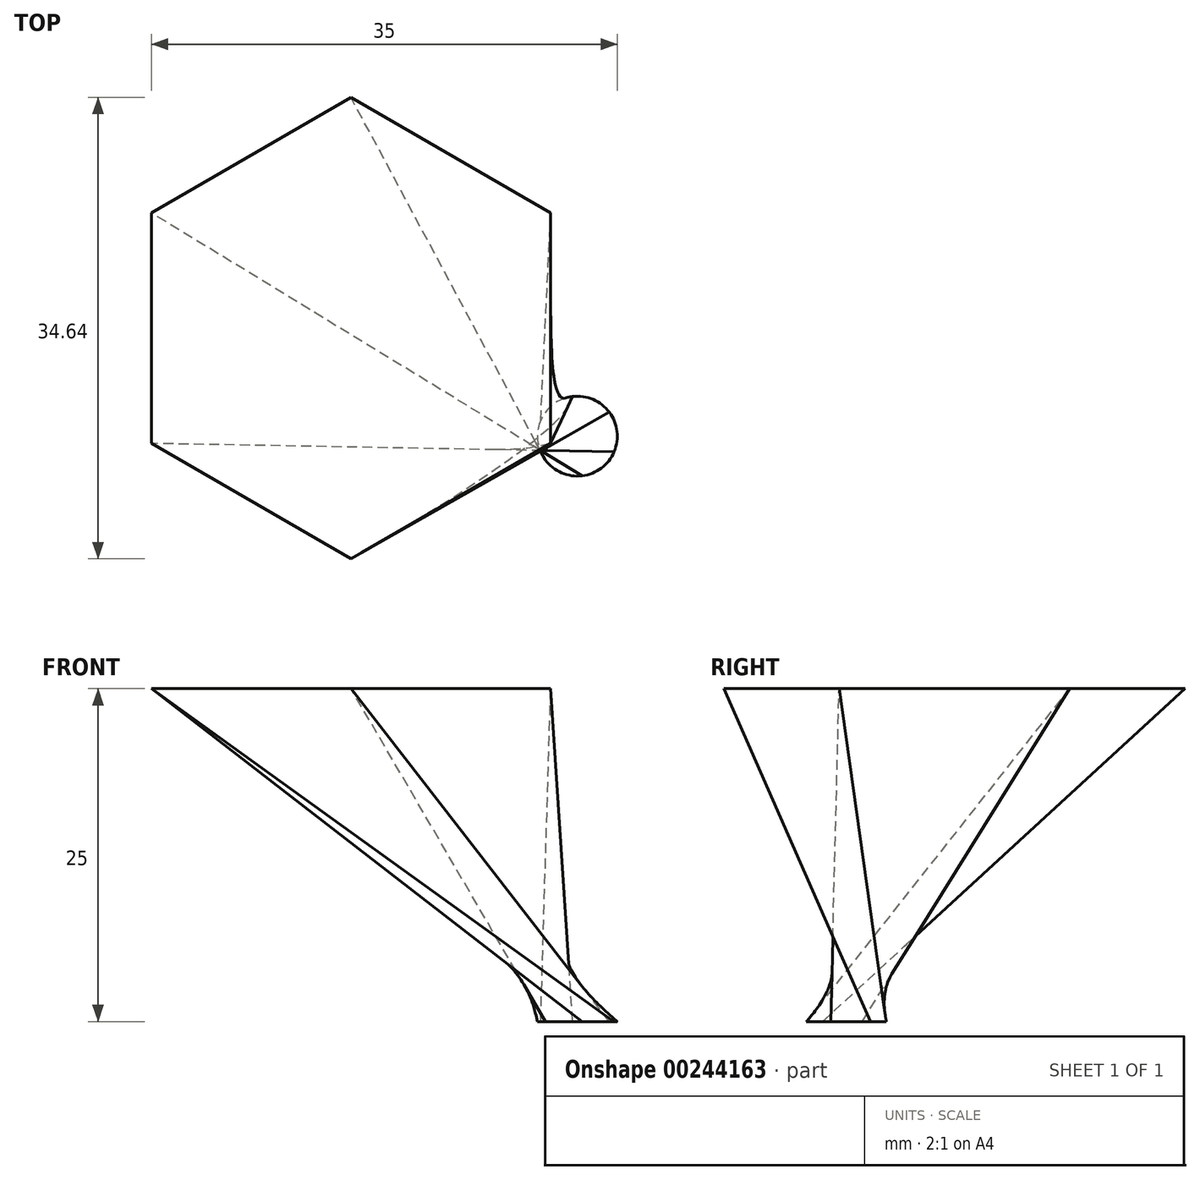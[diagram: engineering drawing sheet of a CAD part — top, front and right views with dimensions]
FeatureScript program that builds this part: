
annotation { "Feature Type Name" : "Feature", "Feature Type Description" : "" }
export const myFeature = defineFeature(function(context is Context, id is Id, definition is map)
    precondition{}
    {
        {
            var Q0;
            Q0=qCreatedBy(makeId("Top.planeOp"),FACE);
            var sketch = newSketch(context, id + "F0", { "sketchPlane" : qUnion([Q0])});
            skCircle(sketch, "E0", {"center": v(17, -8.11) * mm, "radius": 3 * mm});
            skSolve(sketch);
        }
        {
            var Q0;
            Q0=qCreatedBy(makeId("Top.planeOp"),FACE);
            cPlane(context, id + "F1", {"entities" : qUnion([Q0]), "cplaneType" : CPlaneType.OFFSET, "offset" : 25 * mm, "width" : 150 * mm, "height" : 150 * mm});
        }
        {
            var Q0;
            Q0=qCreatedBy(id+"F1.planeOp",FACE);
            var sketch = newSketch(context, id + "F2", { "sketchPlane" : qUnion([Q0])});
            skCircle(sketch, "E1.cCircle", {"center": v(0, 0) * mm, "radius": 15 * mm, "construction": true});
            skLineSegment(sketch, "E1.0", {"start": v(15, 8.66) * mm, "end": v(15, -8.66) * mm});
            skLineSegment(sketch, "E1.1", {"start": v(15, -8.66) * mm, "end": v(0, -17.32) * mm});
            skLineSegment(sketch, "E1.2", {"start": v(0, -17.32) * mm, "end": v(-15, -8.66) * mm});
            skLineSegment(sketch, "E1.3", {"start": v(-15, -8.66) * mm, "end": v(-15, 8.66) * mm});
            skLineSegment(sketch, "E1.4", {"start": v(-15, 8.66) * mm, "end": v(0, 17.32) * mm});
            skLineSegment(sketch, "E1.5", {"start": v(0, 17.32) * mm, "end": v(15, 8.66) * mm});
            skPoint(sketch, "E1.0.midPoint", {"position": v(15, 0) * mm});
            skSolve(sketch);
        }
        {
            var Q0;
            Q0=makeQuery(id+"F0.imprint","IMPRINT",FACE,{"disambiguationData":[TD([[makeQuery(id+"F0.imprint","IMPRINT",EDGE,{"derivedFrom":sQuery(id+"F0.wireOp",EDGE,"E0")}),1.0]])]});
            var Q1;
            Q1=makeQuery(id+"F2.imprint","IMPRINT",FACE,{"disambiguationData":[TD([[makeQuery(id+"F2.imprint","IMPRINT",EDGE,{"derivedFrom":sQuery(id+"F2.wireOp",EDGE,"E1.0")}),-1.0]])]});
            loft(context, id + "F3", {"sheetProfilesArray" : [{ "sheetProfileEntities" : qUnion([Q0]) }, { "sheetProfileEntities" : qUnion([Q1]) }]});
        }
    });
